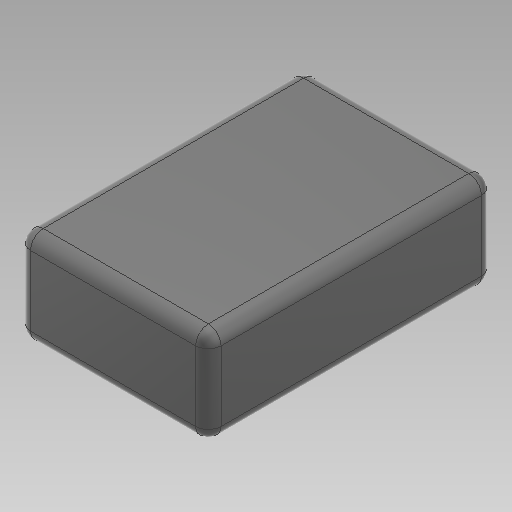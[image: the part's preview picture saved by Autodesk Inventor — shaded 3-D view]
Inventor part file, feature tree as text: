
AUTODESK INVENTOR PART (.ipt)
format: ipt  version: 2020 (Build 240168000, 168)  size: 126,464 bytes
history: native  units: in
note: dims shown in document units (in); Inventor stores cm internally (conversion verified against a paired STEP export)
features: extrude x1, fillet x1, sketch x1
ambient origin geometry x8: Origin, YZ Plane, XZ Plane, XY Plane, X Axis, Y Axis, Z Axis, Center Point
bodies: Solid1 (feature_tree)
feature tree (3):
  extrude  "Extrusion1"  Depth=3.5433in
  fillet  "Fillet1"  Radius=1.1811in
  sketch  "Sketch1"  dims[d0=2.3622in d1=3.5433in d2=1.1811in d3=0.0in d4=0.1575in]
